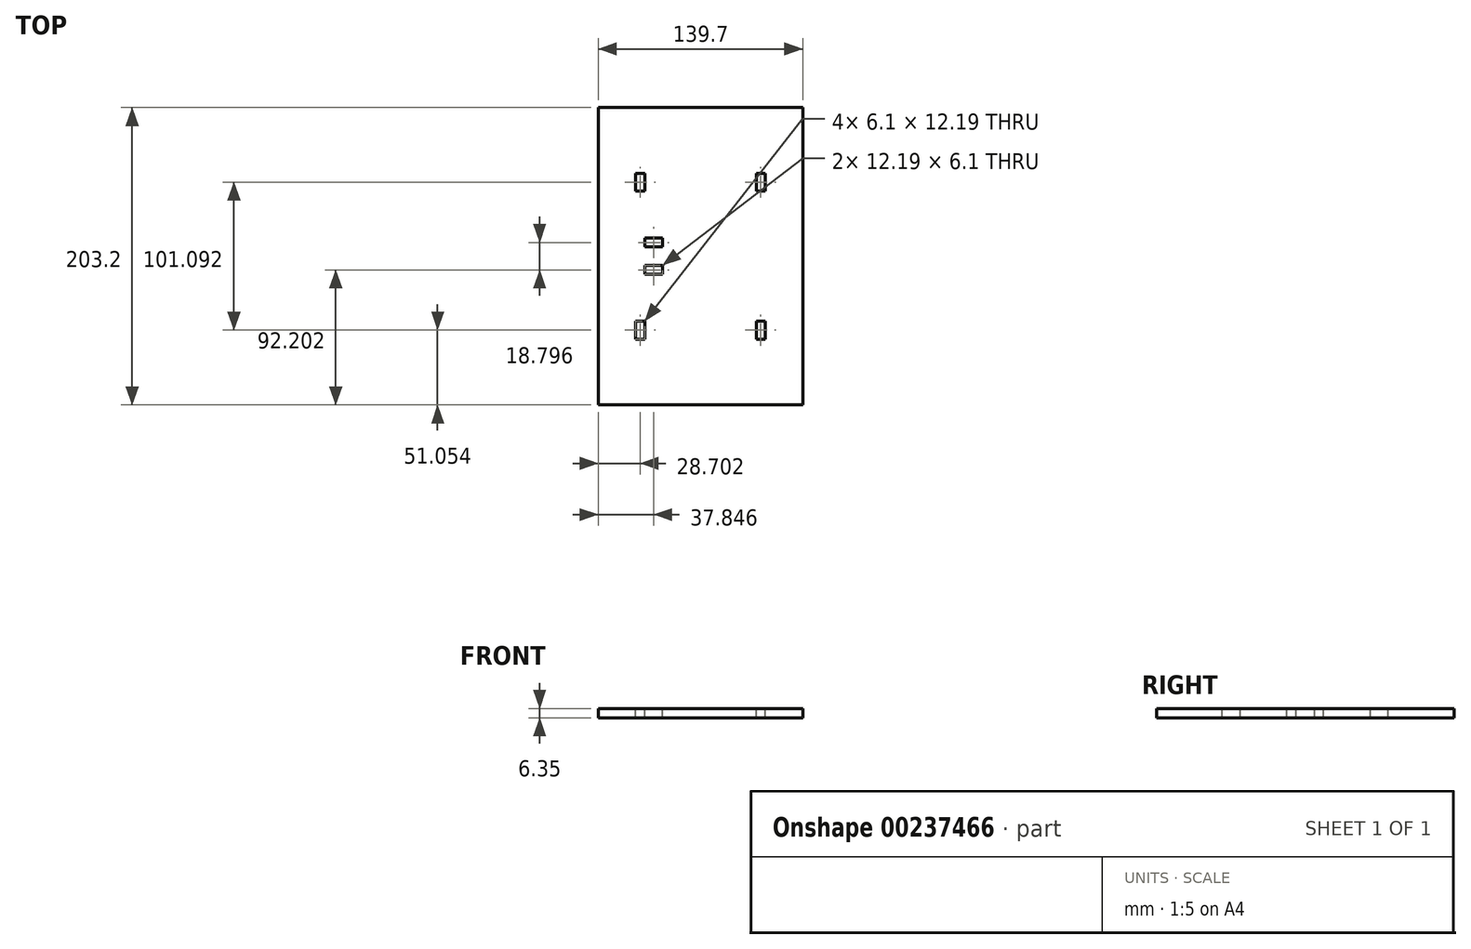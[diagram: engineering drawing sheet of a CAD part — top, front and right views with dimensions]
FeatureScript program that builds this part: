
annotation { "Feature Type Name" : "Feature", "Feature Type Description" : "" }
export const myFeature = defineFeature(function(context is Context, id is Id, definition is map)
    precondition{}
    {
        {
            var Q0;
            Q0=qCreatedBy(makeId("Top.planeOp"),FACE);
            var sketch = newSketch(context, id + "F0", { "sketchPlane" : qUnion([Q0])});
            skLineSegment(sketch, "E0.bottom", {"start": v(69.85, 101.6) * mm, "end": v(-69.85, 101.6) * mm});
            skLineSegment(sketch, "E0.top", {"start": v(69.85, -101.6) * mm, "end": v(-69.85, -101.6) * mm});
            skLineSegment(sketch, "E0.left", {"start": v(69.85, 101.6) * mm, "end": v(69.85, -101.6) * mm});
            skLineSegment(sketch, "E0.right", {"start": v(-69.85, 101.6) * mm, "end": v(-69.85, -101.6) * mm});
            skPoint(sketch, "E0.middle", {"position": v(0, 0) * mm});
            skSolve(sketch);
        }
        {
            var Q0;
            Q0=makeQuery(id+"F0.imprint","IMPRINT",FACE,{"disambiguationData":[TD([[makeQuery(id+"F0.imprint","IMPRINT",EDGE,{"derivedFrom":sQuery(id+"F0.wireOp",EDGE,"E0.bottom")}),1.0]])]});
            extrude(context, id + "F1", {"entities" : qUnion([Q0]), "depth" : 6.35 * mm});
        }
        {
            var Q0;
            Q0=makeQuery(id+"F1.opExtrude","CAP_FACE",FACE,{"disambiguationData":[OSD([sQuery(id+"F0.wireOp",EDGE,"E0.bottom"),sQuery(id+"F0.wireOp",EDGE,"E0.top"),sQuery(id+"F0.wireOp",EDGE,"E0.left"),sQuery(id+"F0.wireOp",EDGE,"E0.right")])],"isStart":false});
            var sketch = newSketch(context, id + "F2", { "sketchPlane" : qUnion([Q0])});
            skLineSegment(sketch, "E1.bottom", {"start": v(-44.2, 56.64) * mm, "end": v(-38.1, 56.64) * mm});
            skLineSegment(sketch, "E1.top", {"start": v(-44.2, 44.45) * mm, "end": v(-38.1, 44.45) * mm});
            skLineSegment(sketch, "E1.left", {"start": v(-44.2, 56.64) * mm, "end": v(-44.2, 44.45) * mm});
            skLineSegment(sketch, "E1.right", {"start": v(-38.1, 56.64) * mm, "end": v(-38.1, 44.45) * mm});
            skLineSegment(sketch, "E2.MirrorCS", {"start": v(44.2, 44.45) * mm, "end": v(38.1, 44.45) * mm});
            skLineSegment(sketch, "E3.MirrorCS", {"start": v(38.1, 56.64) * mm, "end": v(38.1, 44.45) * mm});
            skLineSegment(sketch, "E4.MirrorCS", {"start": v(44.2, 56.64) * mm, "end": v(38.1, 56.64) * mm});
            skLineSegment(sketch, "E5.MirrorCS", {"start": v(44.2, 56.64) * mm, "end": v(44.2, 44.45) * mm});
            skLineSegment(sketch, "E6.MirrorCS", {"start": v(44.2, -56.64) * mm, "end": v(38.1, -56.64) * mm});
            skLineSegment(sketch, "E7.MirrorCS", {"start": v(44.2, -44.45) * mm, "end": v(38.1, -44.45) * mm});
            skLineSegment(sketch, "E8.MirrorCS", {"start": v(-44.2, -56.64) * mm, "end": v(-38.1, -56.64) * mm});
            skLineSegment(sketch, "E9.MirrorCS", {"start": v(-44.2, -44.45) * mm, "end": v(-38.1, -44.45) * mm});
            skLineSegment(sketch, "E10.MirrorCS", {"start": v(38.1, -56.64) * mm, "end": v(38.1, -44.45) * mm});
            skLineSegment(sketch, "E11.MirrorCS", {"start": v(44.2, -56.64) * mm, "end": v(44.2, -44.45) * mm});
            skLineSegment(sketch, "E12.MirrorCS", {"start": v(-38.1, -56.64) * mm, "end": v(-38.1, -44.45) * mm});
            skLineSegment(sketch, "E13.MirrorCS", {"start": v(-44.2, -56.64) * mm, "end": v(-44.2, -44.45) * mm});
            skLineSegment(sketch, "E14.bottom", {"start": v(-38.1, 12.45) * mm, "end": v(-25.9, 12.45) * mm});
            skLineSegment(sketch, "E14.top", {"start": v(-38.1, 6.35) * mm, "end": v(-25.9, 6.35) * mm});
            skLineSegment(sketch, "E14.left", {"start": v(-38.1, 12.45) * mm, "end": v(-38.1, 6.35) * mm});
            skLineSegment(sketch, "E14.right", {"start": v(-25.9, 12.45) * mm, "end": v(-25.9, 6.35) * mm});
            skLineSegment(sketch, "E15.MirrorCS", {"start": v(-38.1, -12.45) * mm, "end": v(-38.1, -6.35) * mm});
            skLineSegment(sketch, "E16.MirrorCS", {"start": v(-38.1, -12.45) * mm, "end": v(-25.9, -12.45) * mm});
            skLineSegment(sketch, "E17.MirrorCS", {"start": v(-25.9, -12.45) * mm, "end": v(-25.9, -6.35) * mm});
            skLineSegment(sketch, "E18.MirrorCS", {"start": v(-38.1, -6.35) * mm, "end": v(-25.9, -6.35) * mm});
            skSolve(sketch);
        }
        {
            var Q0;
            Q0 = qSketchRegion(id + "F2", true);
            extrude(context, id + "F3", {"entities" : qUnion([Q0]), "operationType" : NewBodyOperationType.REMOVE, "oppositeDirection" : true, "depth" : 12.7 * mm});
        }
    });
